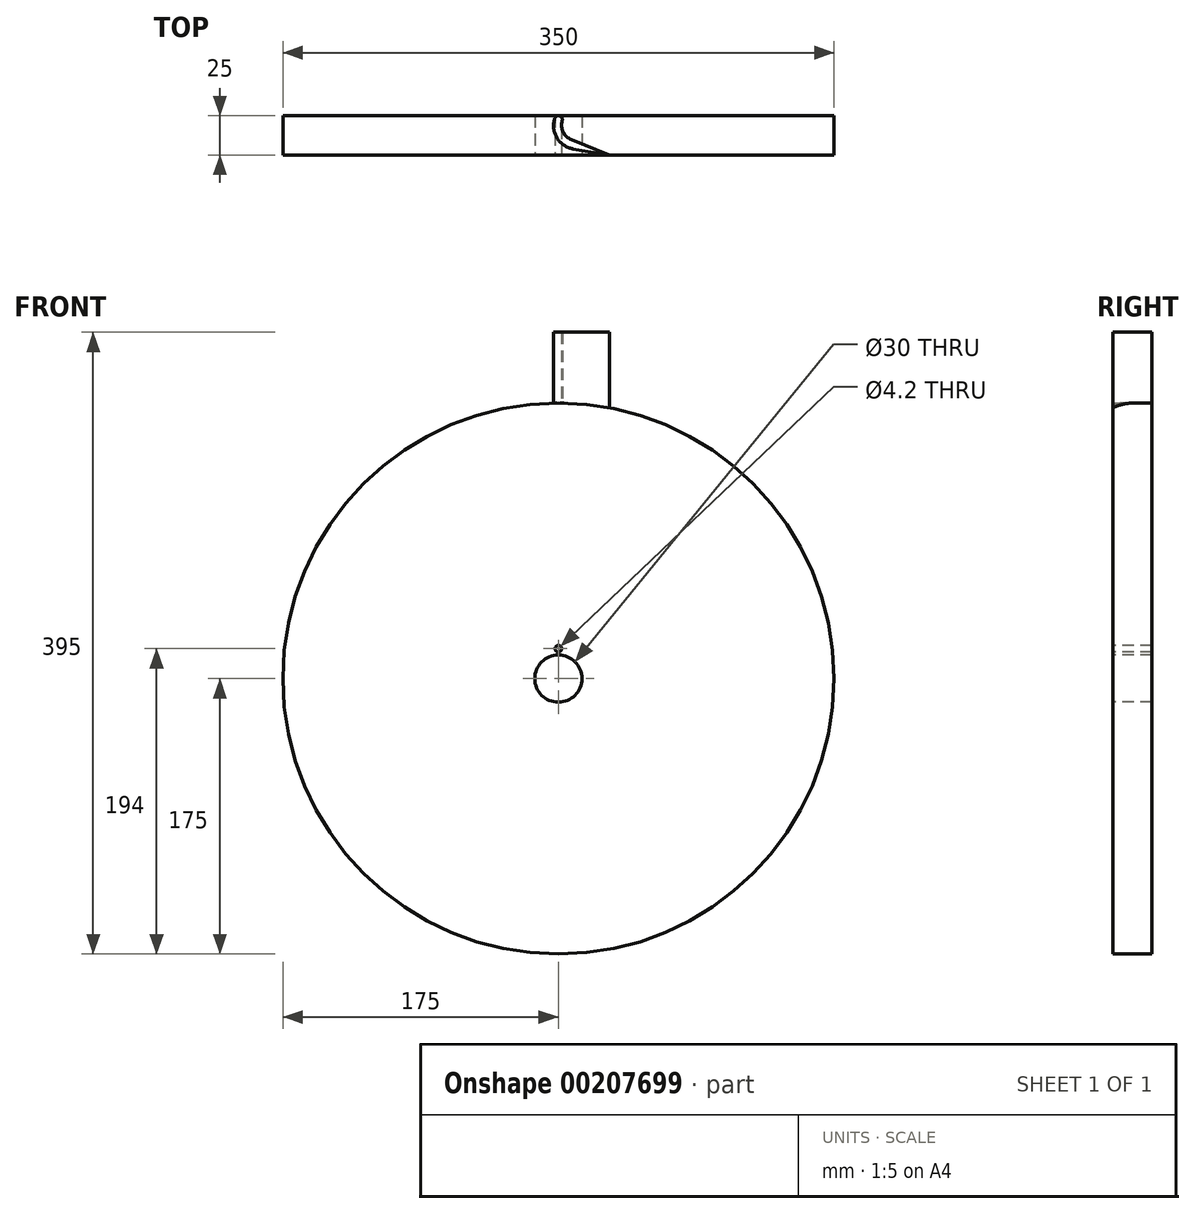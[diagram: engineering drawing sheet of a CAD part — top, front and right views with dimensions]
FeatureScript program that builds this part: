
annotation { "Feature Type Name" : "Feature", "Feature Type Description" : "" }
export const myFeature = defineFeature(function(context is Context, id is Id, definition is map)
    precondition{}
    {
        {
            var Q0;
            Q0=qCreatedBy(makeId("Front.planeOp"),FACE);
            var sketch = newSketch(context, id + "F0", { "sketchPlane" : qUnion([Q0])});
            skCircle(sketch, "E0", {"center": v(0, 0) * mm, "radius": 175 * mm});
            skSolve(sketch);
        }
        {
            var Q0;
            Q0 = qSketchRegion(id + "F0", true);
            extrude(context, id + "F1", {"entities" : qUnion([Q0]), "endBound" : BoundingType.SYMMETRIC, "depth" : 25 * mm});
        }
        {
            var Q0;
            Q0=qCreatedBy(makeId("Top.planeOp"),FACE);
            var sketch = newSketch(context, id + "F2", { "sketchPlane" : qUnion([Q0])});
            skLineSegment(sketch, "E1", {"start": v(0, 12.5) * mm, "end": v(0, -12.5) * mm, "construction": true});
            skCircle(sketch, "E2", {"center": v(0, 10) * mm, "radius": 2.5 * mm, "construction": true});
            skLineSegment(sketch, "E3", {"start": v(0, 0) * mm, "end": v(5.1, 0) * mm, "construction": true});
            skLineSegment(sketch, "E4", {"start": v(0, 10) * mm, "end": v(5.1, 0) * mm, "construction": true});
            skLineSegment(sketch, "E5", {"start": v(5.1, 0) * mm, "end": v(-25.84, -12.5) * mm, "construction": true});
            skLineSegment(sketch, "E6", {"start": v(-8.27, -2.7) * mm, "end": v(-32.52, -12.5) * mm, "construction": true});
            skPoint(sketch, "E7.visualSharp", {"position": v(1.63, 1.3) * mm});
            skArc(sketch, "E7.filletArc", {"start": v(-8.27, -2.7) * mm, "mid": v(-3.03, 2.18) * mm, "end": v(-2.4, 9.31) * mm, "construction": true});
            skPoint(sketch, "E8.visualSharp", {"position": v(9.7, -0.05) * mm});
            skArc(sketch, "E8.filletArc", {"start": v(-9.4, -8.55) * mm, "mid": v(0.89, -1.58) * mm, "end": v(2.38, 10.75) * mm, "construction": true});
            skLineSegment(sketch, "E9", {"start": v(-32.52, -12.5) * mm, "end": v(-25.84, -12.5) * mm});
            skLineSegment(sketch, "E10", {"start": v(-9.4, -8.55) * mm, "end": v(-32.52, -12.5) * mm, "construction": true});
            skCircle(sketch, "E11.MirrorC", {"center": v(0, 10) * mm, "radius": 2.5 * mm});
            skArc(sketch, "E12.MirrorCS", {"start": v(9.4, -8.55) * mm, "mid": v(-0.89, -1.58) * mm, "end": v(-2.38, 10.75) * mm});
            skArc(sketch, "E13.MirrorCS", {"start": v(8.27, -2.7) * mm, "mid": v(3.03, 2.18) * mm, "end": v(2.4, 9.31) * mm});
            skLineSegment(sketch, "E14.MirrorCS", {"start": v(8.27, -2.7) * mm, "end": v(32.52, -12.5) * mm});
            skLineSegment(sketch, "E15.MirrorCS", {"start": v(9.4, -8.55) * mm, "end": v(32.52, -12.5) * mm});
            skSolve(sketch);
        }
        {
            var Q0;
            Q0=makeQuery(id+"F1.opExtrude","CAP_FACE",FACE,{"disambiguationData":[OSD([sQuery(id+"F0.wireOp",EDGE,"E0")])],"isStart":false});
            var sketch = newSketch(context, id + "F3", { "sketchPlane" : qUnion([Q0])});
            skCircle(sketch, "E16", {"center": v(0, 0) * mm, "radius": 15 * mm});
            skSolve(sketch);
        }
        {
            var Q0;
            Q0 = qSketchRegion(id + "F2", true);
            extrude(context, id + "F4", {"entities" : qUnion([Q0]), "operationType" : NewBodyOperationType.ADD, "depth" : 220 * mm});
        }
        {
            var Q0;
            Q0=makeQuery(id+"F3.imprint","IMPRINT",FACE,{"disambiguationData":[TD([[makeQuery(id+"F3.imprint","IMPRINT",EDGE,{"derivedFrom":sQuery(id+"F3.wireOp",EDGE,"E16")}),1.0]])]});
            extrude(context, id + "F5", {"entities" : qUnion([Q0]), "operationType" : NewBodyOperationType.REMOVE, "endBound" : BoundingType.THROUGH_ALL, "oppositeDirection" : true, "depth" : 25 * mm});
        }
        {
            var Q0;
            Q0=makeQuery(id+"F1.opExtrude","CAP_FACE",FACE,{"disambiguationData":[OSD([sQuery(id+"F0.wireOp",EDGE,"E0")])],"isStart":false});
            var sketch = newSketch(context, id + "F6", { "sketchPlane" : qUnion([Q0])});
            skCircle(sketch, "E17", {"center": v(0, 19) * mm, "radius": 2.5 * mm});
            skSolve(sketch);
        }
        {
            var Q0;
            Q0=sQuery(id+"F6.wireOp",VERTEX,"E17.center");
            var Q1;
            Q1=makeQuery(id+"F1.opExtrude","SWEPT_BODY",BODY,{"disambiguationData":[OSD([sQuery(id+"F0.wireOp",EDGE,"E0")])]});
            hole(context, id + "F7", {"style" : HoleStyle.SIMPLE, "endStyle" : HoleEndStyle.THROUGH, "standardTappedOrClearance" : lookupTablePath({ "standard" : "ISO", "engagement" : "75%", "pitch" : "0.8 mm", "size" : "M5", "type" : "Tapped" }), "standardBlindInLast" : lookupTablePath({ "standard" : "ISO", "engagement" : "75%", "pitch" : "0.8 mm", "size" : "M5", "type" : "Tapped" }), "holeDiameter" : 4.2 * mm, "showTappedDepth" : true, "tappedDepth" : 12.5 * mm, "tapClearance" : 3, "locations" : qUnion([Q0]), "scope" : qUnion([Q1]), "majorDiameter" : 5 * mm});
        }
    });
